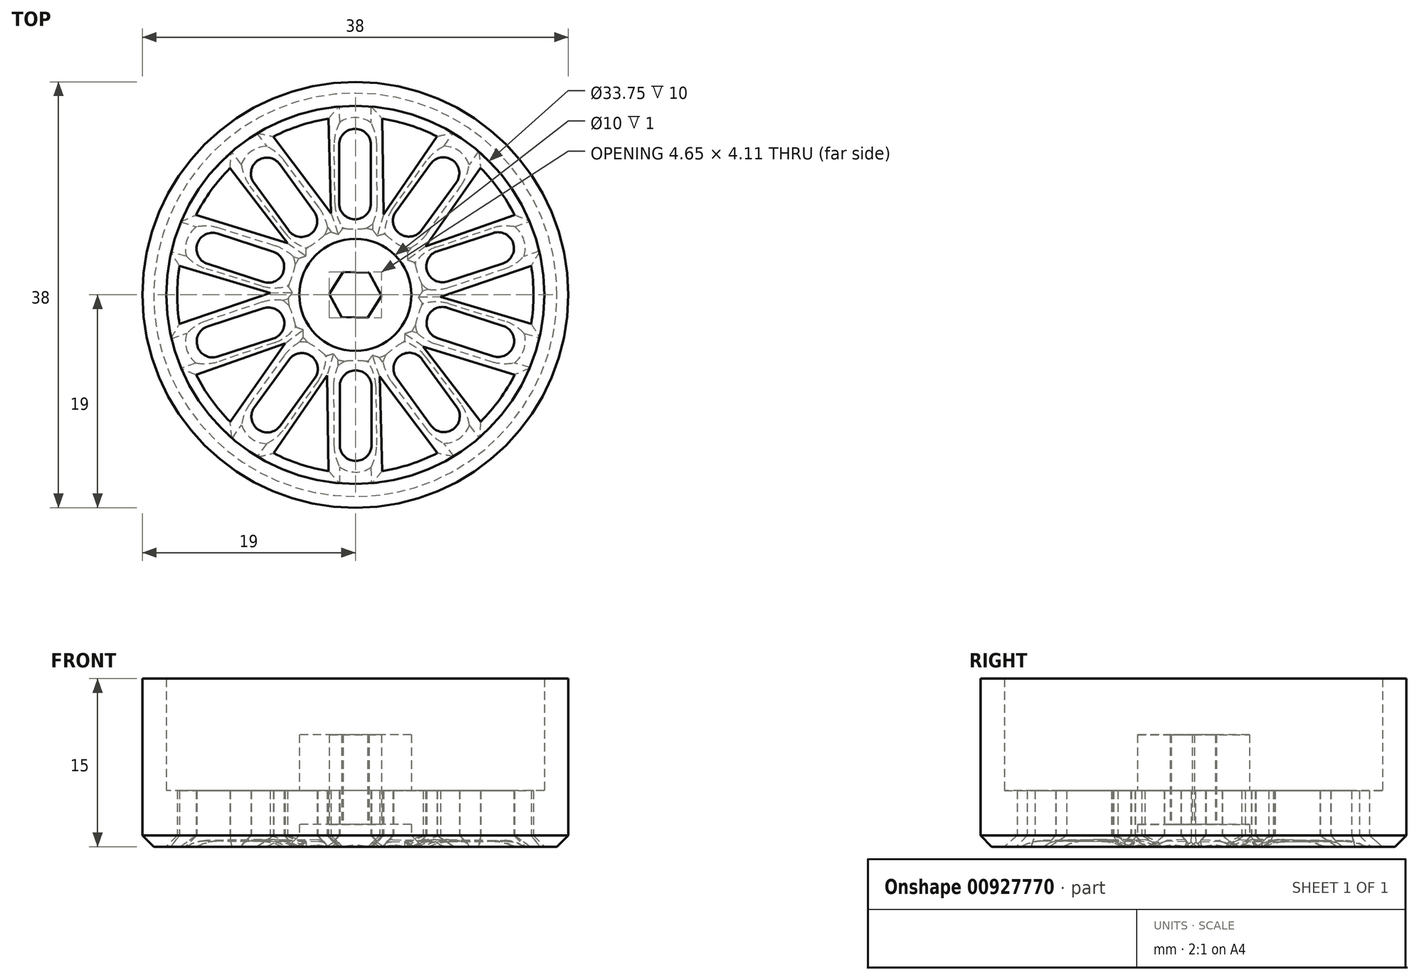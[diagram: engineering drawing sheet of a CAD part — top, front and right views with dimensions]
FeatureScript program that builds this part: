
annotation { "Feature Type Name" : "Feature", "Feature Type Description" : "" }
export const myFeature = defineFeature(function(context is Context, id is Id, definition is map)
    precondition{}
    {
        {
            var Q0;
            Q0=qCreatedBy(makeId("Top.planeOp"),FACE);
            var sketch = newSketch(context, id + "F0", { "sketchPlane" : qUnion([Q0])});
            skCircle(sketch, "E0", {"center": v(0, 0) * mm, "radius": 19 * mm});
            skCircle(sketch, "E1", {"center": v(0, 0) * mm, "radius": 16.88 * mm});
            skCircle(sketch, "E2", {"center": v(0, 0) * mm, "radius": 5 * mm});
            skLineSegment(sketch, "E3", {"start": v(0, 5) * mm, "end": v(0, 16.88) * mm, "construction": true});
            skPoint(sketch, "E4", {"position": v(0, 10.94) * mm});
            skCircle(sketch, "E5", {"center": v(-14.8, 19.1) * mm, "radius": 2.5 * mm});
            skLineSegment(sketch, "E6", {"start": v(-17.26, 19.52) * mm, "end": v(-12.33, 19.52) * mm, "construction": true});
            skLineSegment(sketch, "E7", {"start": v(-15.14, 26.3) * mm, "end": v(-17.26, 19.52) * mm});
            skLineSegment(sketch, "E8", {"start": v(-14.18, 26.28) * mm, "end": v(-12.33, 19.52) * mm});
            skArc(sketch, "E9.filletArc", {"start": v(-14.18, 26.28) * mm, "mid": v(-14.66, 26.65) * mm, "end": v(-15.14, 26.3) * mm});
            skLineSegment(sketch, "E10.5.0", {"start": v(19.08, -22.93) * mm, "end": v(14.42, -19.82) * mm});
            skArc(sketch, "E10.5.1", {"start": v(14.42, -19.82) * mm, "mid": v(13.24, -19.67) * mm, "end": v(12.36, -20.48) * mm});
            skLineSegment(sketch, "E10.5.2", {"start": v(10.23, -25.67) * mm, "end": v(12.36, -20.48) * mm});
            skArc(sketch, "E10.5.3", {"start": v(10.23, -25.67) * mm, "mid": v(14.82, -24.84) * mm, "end": v(19.08, -22.93) * mm});
            skPoint(sketch, "E11", {"position": v(0, 15.9) * mm});
            skCircle(sketch, "E12", {"center": v(0, 0) * mm, "radius": 15.9 * mm, "construction": true});
            skCircle(sketch, "E13", {"center": v(0, 0) * mm, "radius": 5.66 * mm, "construction": true});
            skPoint(sketch, "E14.visualSharp", {"position": v(1.68, 5.4) * mm});
            skArc(sketch, "E15.filletArc", {"start": v(15.09, -4.95) * mm, "mid": v(15.14, -4.92) * mm, "end": v(15.12, -4.86) * mm});
            skArc(sketch, "E16.filletArc", {"start": v(15.12, 4.86) * mm, "mid": v(15.14, 4.92) * mm, "end": v(15.09, 4.95) * mm});
            skLineSegment(sketch, "E17.bottom", {"start": v(1, -18.97) * mm, "end": v(-1, -18.97) * mm, "construction": true});
            skLineSegment(sketch, "E17.top", {"start": v(1, -0.03) * mm, "end": v(-1, -0.03) * mm, "construction": true});
            skLineSegment(sketch, "E18", {"start": v(0, 0) * mm, "end": v(0, -5) * mm, "construction": true});
            skLineSegment(sketch, "E19.trimOffspring", {"start": v(0, -16.88) * mm, "end": v(0, -19) * mm, "construction": true});
            skPoint(sketch, "E20.orphan", {"position": v(0.1, -15.9) * mm});
            skLineSegment(sketch, "E21.bottom", {"start": v(1.45, -13.4) * mm, "end": v(-1.4, -13.4) * mm});
            skLineSegment(sketch, "E21.top", {"start": v(1.45, -8.16) * mm, "end": v(-1.4, -8.16) * mm});
            skLineSegment(sketch, "E21.left", {"start": v(1.45, -13.4) * mm, "end": v(1.45, -8.16) * mm});
            skLineSegment(sketch, "E21.right", {"start": v(-1.4, -13.4) * mm, "end": v(-1.4, -8.16) * mm});
            skPoint(sketch, "E21.middle", {"position": v(0.03, -10.78) * mm});
            skPoint(sketch, "E22.end.orphan", {"position": v(-0.05, -5.66) * mm});
            skCircle(sketch, "E23", {"center": v(0.03, -8.16) * mm, "radius": 1.42 * mm});
            skCircle(sketch, "E24", {"center": v(0.03, -13.4) * mm, "radius": 1.42 * mm});
            skCircle(sketch, "E25.1.0", {"center": v(7.9, -10.83) * mm, "radius": 1.42 * mm});
            skLineSegment(sketch, "E25.1.1", {"start": v(6.75, -11.66) * mm, "end": v(3.67, -7.42) * mm});
            skLineSegment(sketch, "E25.1.2", {"start": v(9.05, -10) * mm, "end": v(5.97, -5.75) * mm});
            skLineSegment(sketch, "E25.1.3", {"start": v(5.97, -5.75) * mm, "end": v(3.67, -7.42) * mm});
            skCircle(sketch, "E25.1.4", {"center": v(4.82, -6.59) * mm, "radius": 1.42 * mm});
            skLineSegment(sketch, "E25.1.5", {"start": v(9.05, -10) * mm, "end": v(6.75, -11.66) * mm});
            skCircle(sketch, "E25.2.0", {"center": v(12.75, -4.12) * mm, "radius": 1.42 * mm});
            skLineSegment(sketch, "E25.2.1", {"start": v(12.31, -5.47) * mm, "end": v(7.33, -3.85) * mm});
            skLineSegment(sketch, "E25.2.2", {"start": v(13.2, -2.77) * mm, "end": v(8.21, -1.15) * mm});
            skLineSegment(sketch, "E25.2.3", {"start": v(8.21, -1.15) * mm, "end": v(7.33, -3.85) * mm});
            skCircle(sketch, "E25.2.4", {"center": v(7.77, -2.5) * mm, "radius": 1.42 * mm});
            skLineSegment(sketch, "E25.2.5", {"start": v(13.2, -2.77) * mm, "end": v(12.31, -5.47) * mm});
            skCircle(sketch, "E25.3.0", {"center": v(12.74, 4.17) * mm, "radius": 1.42 * mm});
            skLineSegment(sketch, "E25.3.1", {"start": v(13.18, 2.82) * mm, "end": v(8.2, 1.2) * mm});
            skLineSegment(sketch, "E25.3.2", {"start": v(12.3, 5.52) * mm, "end": v(7.32, 3.9) * mm});
            skLineSegment(sketch, "E25.3.3", {"start": v(7.32, 3.9) * mm, "end": v(8.2, 1.2) * mm});
            skCircle(sketch, "E25.3.4", {"center": v(7.76, 2.55) * mm, "radius": 1.42 * mm});
            skLineSegment(sketch, "E25.3.5", {"start": v(12.3, 5.52) * mm, "end": v(13.18, 2.82) * mm});
            skCircle(sketch, "E25.4.0", {"center": v(7.86, 10.86) * mm, "radius": 1.42 * mm});
            skLineSegment(sketch, "E25.4.1", {"start": v(9, 10.02) * mm, "end": v(5.93, 5.78) * mm});
            skLineSegment(sketch, "E25.4.2", {"start": v(6.7, 11.7) * mm, "end": v(3.63, 7.45) * mm});
            skLineSegment(sketch, "E25.4.3", {"start": v(3.63, 7.45) * mm, "end": v(5.93, 5.78) * mm});
            skCircle(sketch, "E25.4.4", {"center": v(4.78, 6.62) * mm, "radius": 1.42 * mm});
            skLineSegment(sketch, "E25.4.5", {"start": v(6.7, 11.7) * mm, "end": v(9, 10.02) * mm});
            skCircle(sketch, "E25.5.0", {"center": v(-0.03, 13.4) * mm, "radius": 1.42 * mm});
            skLineSegment(sketch, "E25.5.1", {"start": v(1.4, 13.4) * mm, "end": v(1.4, 8.16) * mm});
            skLineSegment(sketch, "E25.5.2", {"start": v(-1.45, 13.4) * mm, "end": v(-1.45, 8.16) * mm});
            skLineSegment(sketch, "E25.5.3", {"start": v(-1.45, 8.16) * mm, "end": v(1.4, 8.16) * mm});
            skCircle(sketch, "E25.5.4", {"center": v(-0.03, 8.16) * mm, "radius": 1.42 * mm});
            skLineSegment(sketch, "E25.5.5", {"start": v(-1.45, 13.4) * mm, "end": v(1.4, 13.4) * mm});
            skCircle(sketch, "E25.6.0", {"center": v(-7.9, 10.83) * mm, "radius": 1.42 * mm});
            skLineSegment(sketch, "E25.6.1", {"start": v(-6.75, 11.66) * mm, "end": v(-3.67, 7.42) * mm});
            skLineSegment(sketch, "E25.6.2", {"start": v(-9.05, 10) * mm, "end": v(-5.97, 5.75) * mm});
            skLineSegment(sketch, "E25.6.3", {"start": v(-5.97, 5.75) * mm, "end": v(-3.67, 7.42) * mm});
            skCircle(sketch, "E25.6.4", {"center": v(-4.82, 6.59) * mm, "radius": 1.42 * mm});
            skLineSegment(sketch, "E25.6.5", {"start": v(-9.05, 10) * mm, "end": v(-6.75, 11.66) * mm});
            skCircle(sketch, "E25.7.0", {"center": v(-12.75, 4.12) * mm, "radius": 1.42 * mm});
            skLineSegment(sketch, "E25.7.1", {"start": v(-12.31, 5.47) * mm, "end": v(-7.33, 3.85) * mm});
            skLineSegment(sketch, "E25.7.2", {"start": v(-13.2, 2.77) * mm, "end": v(-8.21, 1.15) * mm});
            skLineSegment(sketch, "E25.7.3", {"start": v(-8.21, 1.15) * mm, "end": v(-7.33, 3.85) * mm});
            skCircle(sketch, "E25.7.4", {"center": v(-7.77, 2.5) * mm, "radius": 1.42 * mm});
            skLineSegment(sketch, "E25.7.5", {"start": v(-13.2, 2.77) * mm, "end": v(-12.31, 5.47) * mm});
            skCircle(sketch, "E25.8.0", {"center": v(-12.74, -4.17) * mm, "radius": 1.42 * mm});
            skLineSegment(sketch, "E25.8.1", {"start": v(-13.18, -2.82) * mm, "end": v(-8.2, -1.2) * mm});
            skLineSegment(sketch, "E25.8.2", {"start": v(-12.3, -5.52) * mm, "end": v(-7.32, -3.9) * mm});
            skLineSegment(sketch, "E25.8.3", {"start": v(-7.32, -3.9) * mm, "end": v(-8.2, -1.2) * mm});
            skCircle(sketch, "E25.8.4", {"center": v(-7.76, -2.55) * mm, "radius": 1.42 * mm});
            skLineSegment(sketch, "E25.8.5", {"start": v(-12.3, -5.52) * mm, "end": v(-13.18, -2.82) * mm});
            skLineSegment(sketch, "E26.2.9.0", {"start": v(-9, -10.02) * mm, "end": v(-5.93, -5.78) * mm});
            skCircle(sketch, "E26.3.9.0", {"center": v(-7.86, -10.86) * mm, "radius": 1.42 * mm});
            skLineSegment(sketch, "E26.5.9.0", {"start": v(-6.7, -11.7) * mm, "end": v(-3.63, -7.45) * mm});
            skLineSegment(sketch, "E26.8.9.0", {"start": v(-3.63, -7.45) * mm, "end": v(-5.93, -5.78) * mm});
            skCircle(sketch, "E26.11.9.0", {"center": v(-4.78, -6.62) * mm, "radius": 1.42 * mm});
            skLineSegment(sketch, "E26.13.9.0", {"start": v(-6.7, -11.7) * mm, "end": v(-9, -10.02) * mm});
            skArc(sketch, "E27", {"start": v(-7.3, -14.13) * mm, "mid": v(-4.9, -15.12) * mm, "end": v(-2.39, -15.72) * mm});
            skLineSegment(sketch, "E28", {"start": v(-7.3, -14.13) * mm, "end": v(-2.52, -7.18) * mm});
            skLineSegment(sketch, "E29", {"start": v(-2.52, -7.18) * mm, "end": v(-2.39, -15.72) * mm});
            skLineSegment(sketch, "E30.1.0", {"start": v(2.18, -7.3) * mm, "end": v(7.31, -14.12) * mm});
            skLineSegment(sketch, "E30.1.1", {"start": v(2.4, -15.72) * mm, "end": v(2.18, -7.3) * mm});
            skArc(sketch, "E30.1.2", {"start": v(2.4, -15.72) * mm, "mid": v(4.92, -15.12) * mm, "end": v(7.31, -14.12) * mm});
            skLineSegment(sketch, "E30.2.0", {"start": v(6.05, -4.62) * mm, "end": v(14.22, -7.13) * mm});
            skLineSegment(sketch, "E30.2.1", {"start": v(11.18, -11.3) * mm, "end": v(6.05, -4.62) * mm});
            skArc(sketch, "E30.2.2", {"start": v(11.18, -11.3) * mm, "mid": v(12.86, -9.34) * mm, "end": v(14.22, -7.13) * mm});
            skLineSegment(sketch, "E30.3.0", {"start": v(7.61, -0.18) * mm, "end": v(15.7, 2.6) * mm});
            skLineSegment(sketch, "E30.3.1", {"start": v(15.7, -2.58) * mm, "end": v(7.61, -0.18) * mm});
            skArc(sketch, "E30.3.2", {"start": v(15.7, -2.58) * mm, "mid": v(15.9, 0) * mm, "end": v(15.7, 2.6) * mm});
            skLineSegment(sketch, "E30.4.0", {"start": v(6.26, 4.33) * mm, "end": v(11.17, 11.32) * mm});
            skLineSegment(sketch, "E30.4.1", {"start": v(14.21, 7.14) * mm, "end": v(6.26, 4.33) * mm});
            skArc(sketch, "E30.4.2", {"start": v(14.21, 7.14) * mm, "mid": v(12.86, 9.35) * mm, "end": v(11.17, 11.32) * mm});
            skLineSegment(sketch, "E30.5.0", {"start": v(2.52, 7.18) * mm, "end": v(2.39, 15.72) * mm});
            skLineSegment(sketch, "E30.5.1", {"start": v(7.3, 14.13) * mm, "end": v(2.52, 7.18) * mm});
            skArc(sketch, "E30.5.2", {"start": v(7.3, 14.13) * mm, "mid": v(4.9, 15.12) * mm, "end": v(2.39, 15.72) * mm});
            skLineSegment(sketch, "E30.6.0", {"start": v(-2.18, 7.3) * mm, "end": v(-7.31, 14.12) * mm});
            skLineSegment(sketch, "E30.6.1", {"start": v(-2.4, 15.72) * mm, "end": v(-2.18, 7.3) * mm});
            skArc(sketch, "E30.6.2", {"start": v(-2.4, 15.72) * mm, "mid": v(-4.92, 15.12) * mm, "end": v(-7.31, 14.12) * mm});
            skLineSegment(sketch, "E30.7.0", {"start": v(-6.05, 4.62) * mm, "end": v(-14.22, 7.13) * mm});
            skLineSegment(sketch, "E30.7.1", {"start": v(-11.18, 11.3) * mm, "end": v(-6.05, 4.62) * mm});
            skArc(sketch, "E30.7.2", {"start": v(-11.18, 11.3) * mm, "mid": v(-12.86, 9.34) * mm, "end": v(-14.22, 7.13) * mm});
            skLineSegment(sketch, "E30.8.0", {"start": v(-7.61, 0.18) * mm, "end": v(-15.7, -2.6) * mm});
            skLineSegment(sketch, "E30.8.1", {"start": v(-15.7, 2.58) * mm, "end": v(-7.61, 0.18) * mm});
            skArc(sketch, "E30.8.2", {"start": v(-15.7, 2.58) * mm, "mid": v(-15.9, 0) * mm, "end": v(-15.7, -2.6) * mm});
            skLineSegment(sketch, "E30.9.0", {"start": v(-6.26, -4.33) * mm, "end": v(-11.17, -11.32) * mm});
            skLineSegment(sketch, "E30.9.1", {"start": v(-14.21, -7.14) * mm, "end": v(-6.26, -4.33) * mm});
            skArc(sketch, "E30.9.2", {"start": v(-14.21, -7.14) * mm, "mid": v(-12.86, -9.35) * mm, "end": v(-11.17, -11.32) * mm});
            skSolve(sketch);
        }
        {
            var Q0;
            Q0=makeQuery(id+"F0.imprint","IMPRINT",FACE,{"disambiguationData":[TD([[makeQuery(id+"F0.imprint","IMPRINT",EDGE,{"derivedFrom":sQuery(id+"F0.wireOp",EDGE,"E0")}),1.0]])]});
            extrude(context, id + "F1", {"entities" : qUnion([Q0]), "depth" : 15 * mm, "offsetDistance" : 25 * mm});
        }
        {
            var Q0;
            Q0=makeQuery(id+"F0.imprint","IMPRINT",FACE,{"disambiguationData":[TD([[makeQuery(id+"F0.imprint","IMPRINT",EDGE,{"derivedFrom":sQuery(id+"F0.wireOp",EDGE,"E1")}),1.0]])]});
            extrude(context, id + "F2", {"entities" : qUnion([Q0]), "operationType" : NewBodyOperationType.ADD, "depth" : 5 * mm, "offsetDistance" : 25 * mm});
        }
        {
            var Q0;
            {var subQ0=sQuery(id+"F0.wireOp",EDGE,"E2");var subQ1=makeQuery(id+"F0.imprint","INTERSECT",VERTEX,{"derivedFrom":[subQ0,sQuery(id+"F0.wireOp",EDGE,"FMw9U3Ag-M4uU-eOUw-AIyu-Y3kzjyrUIhWa.right")]});Q0=makeQuery(id+"F0.imprint","IMPRINT",FACE,{"disambiguationData":[TD([[makeQuery(id+"F0.imprint","IMPRINT",EDGE,{"disambiguationData":[TD([[subQ1,1.0]])],"derivedFrom":subQ0}),1.0]])]});}
            extrude(context, id + "F3", {"entities" : qUnion([Q0]), "operationType" : NewBodyOperationType.ADD, "depth" : 10 * mm, "offsetDistance" : 25 * mm});
        }
        {
            var Q0;
            Q0=makeQuery(id+"F0.imprint","IMPRINT",FACE,{"disambiguationData":[TD([[makeQuery(id+"F0.imprint","IMPRINT",EDGE,{"derivedFrom":sQuery(id+"F0.wireOp",EDGE,"E2")}),1.0]])]});
            extrude(context, id + "F4", {"entities" : qUnion([Q0]), "operationType" : NewBodyOperationType.REMOVE, "depth" : 2 * mm, "offsetDistance" : 25 * mm});
        }
        {
            var Q0;
            Q0=makeQuery(id+"F0.imprint","IMPRINT",FACE,{"disambiguationData":[TD([[makeQuery(id+"F0.imprint","IMPRINT",EDGE,{"derivedFrom":sQuery(id+"F0.wireOp",EDGE,"E2")}),1.0]])]});
            var sketch = newSketch(context, id + "F5", { "sketchPlane" : qUnion([Q0])});
            skPoint(sketch, "E31.0.midPoint", {"position": v(-1.32, 0.78) * mm});
            skCircle(sketch, "E32.cCircle", {"center": v(0, 0) * mm, "radius": 2.02 * mm, "construction": true});
            skLineSegment(sketch, "E32.0", {"start": v(-2.33, 0.08) * mm, "end": v(-1.1, 2.06) * mm});
            skLineSegment(sketch, "E32.1", {"start": v(-1.1, 2.06) * mm, "end": v(1.24, 1.97) * mm});
            skLineSegment(sketch, "E32.2", {"start": v(1.24, 1.97) * mm, "end": v(2.33, -0.08) * mm});
            skLineSegment(sketch, "E32.3", {"start": v(2.33, -0.08) * mm, "end": v(1.1, -2.06) * mm});
            skLineSegment(sketch, "E32.4", {"start": v(1.1, -2.06) * mm, "end": v(-1.24, -1.97) * mm});
            skLineSegment(sketch, "E32.5", {"start": v(-1.24, -1.97) * mm, "end": v(-2.33, 0.08) * mm});
            skPoint(sketch, "E32.0.midPoint", {"position": v(-1.7, 1.07) * mm});
            skPoint(sketch, "E33.orphan", {"position": v(-0.9, -1.52) * mm});
            skPoint(sketch, "E34.orphan", {"position": v(0.87, -1.54) * mm});
            skPoint(sketch, "E35.orphan", {"position": v(-1.77, 0.02) * mm});
            skPoint(sketch, "E31.1.start.orphan", {"position": v(-0.87, 1.54) * mm});
            skCircle(sketch, "E36.cCircle", {"center": v(0, -5.83) * mm, "radius": 1.3 * mm, "construction": true});
            skLineSegment(sketch, "E36.0", {"start": v(0.95, -7.14) * mm, "end": v(-0.95, -7.14) * mm});
            skLineSegment(sketch, "E36.1", {"start": v(-0.95, -7.14) * mm, "end": v(-1.54, -5.33) * mm});
            skLineSegment(sketch, "E36.2", {"start": v(-1.54, -5.33) * mm, "end": v(0, -4.21) * mm});
            skLineSegment(sketch, "E36.3", {"start": v(0, -4.21) * mm, "end": v(1.54, -5.33) * mm});
            skLineSegment(sketch, "E36.4", {"start": v(1.54, -5.33) * mm, "end": v(0.95, -7.14) * mm});
            skPoint(sketch, "E36.0.midPoint", {"position": v(0, -7.14) * mm});
            skLineSegment(sketch, "E37.1.0", {"start": v(5.54, -0.18) * mm, "end": v(7.08, -1.3) * mm});
            skLineSegment(sketch, "E37.1.1", {"start": v(4, -1.3) * mm, "end": v(5.54, -0.18) * mm});
            skLineSegment(sketch, "E37.1.2", {"start": v(4.6, -3.11) * mm, "end": v(4, -1.3) * mm});
            skLineSegment(sketch, "E37.1.3", {"start": v(6.5, -3.11) * mm, "end": v(4.6, -3.11) * mm});
            skLineSegment(sketch, "E37.1.4", {"start": v(7.08, -1.3) * mm, "end": v(6.5, -3.11) * mm});
            skLineSegment(sketch, "E37.2.0", {"start": v(1.89, 5.22) * mm, "end": v(3.43, 6.33) * mm});
            skLineSegment(sketch, "E37.2.1", {"start": v(2.47, 3.4) * mm, "end": v(1.89, 5.22) * mm});
            skLineSegment(sketch, "E37.2.2", {"start": v(4.38, 3.4) * mm, "end": v(2.47, 3.4) * mm});
            skLineSegment(sketch, "E37.2.3", {"start": v(4.97, 5.22) * mm, "end": v(4.38, 3.4) * mm});
            skLineSegment(sketch, "E37.2.4", {"start": v(3.43, 6.33) * mm, "end": v(4.97, 5.22) * mm});
            skLineSegment(sketch, "E37.3.0", {"start": v(-4.38, 3.4) * mm, "end": v(-4.97, 5.22) * mm});
            skLineSegment(sketch, "E37.3.1", {"start": v(-2.47, 3.4) * mm, "end": v(-4.38, 3.4) * mm});
            skLineSegment(sketch, "E37.3.2", {"start": v(-1.89, 5.22) * mm, "end": v(-2.47, 3.4) * mm});
            skLineSegment(sketch, "E37.3.3", {"start": v(-3.43, 6.33) * mm, "end": v(-1.89, 5.22) * mm});
            skLineSegment(sketch, "E37.3.4", {"start": v(-4.97, 5.22) * mm, "end": v(-3.43, 6.33) * mm});
            skLineSegment(sketch, "E37.4.0", {"start": v(-4.6, -3.11) * mm, "end": v(-6.5, -3.11) * mm});
            skLineSegment(sketch, "E37.4.1", {"start": v(-4, -1.3) * mm, "end": v(-4.6, -3.11) * mm});
            skLineSegment(sketch, "E37.4.2", {"start": v(-5.54, -0.18) * mm, "end": v(-4, -1.3) * mm});
            skLineSegment(sketch, "E37.4.3", {"start": v(-7.08, -1.3) * mm, "end": v(-5.54, -0.18) * mm});
            skLineSegment(sketch, "E37.4.4", {"start": v(-6.5, -3.11) * mm, "end": v(-7.08, -1.3) * mm});
            skSolve(sketch);
        }
        {
            var Q0;
            Q0=makeQuery(id+"F5.imprint","IMPRINT",FACE,{"disambiguationData":[TD([[makeQuery(id+"F5.imprint","IMPRINT",EDGE,{"derivedFrom":sQuery(id+"F5.wireOp",EDGE,"E32.0")}),-1.0]])]});
            extrude(context, id + "F6", {"entities" : qUnion([Q0]), "operationType" : NewBodyOperationType.REMOVE, "depth" : 25 * mm, "offsetDistance" : 25 * mm});
        }
        {
            var Q0;
            {var subQ0=sQuery(id+"F0.wireOp",EDGE,"E2");var subQ1=sQuery(id+"F0.wireOp",EDGE,"E1");Q0=makeQuery(id+"F3.boolean.opBoolean","MERGE",FACE,{"derivedFrom":[makeQuery(id+"F2.boolean.opBoolean","MERGE",FACE,{"derivedFrom":[makeQuery(id+"F1.opExtrude","CAP_FACE",FACE,{"disambiguationData":[OSD([sQuery(id+"F0.wireOp",EDGE,"E0"),subQ1])],"isStart":true}),makeQuery(id+"F2.opExtrude","CAP_FACE",FACE,{"disambiguationData":[OSD([subQ1,subQ0,sQuery(id+"F0.wireOp",EDGE,"E5"),sQuery(id+"F0.wireOp",EDGE,"E7"),sQuery(id+"F0.wireOp",EDGE,"E8"),sQuery(id+"F0.wireOp",EDGE,"E9.filletArc"),sQuery(id+"F0.wireOp",EDGE,"1d552ee7-da9b-4f0c-a288-42d00aae1e59.1.0"),sQuery(id+"F0.wireOp",EDGE,"1d552ee7-da9b-4f0c-a288-42d00aae1e59.1.1"),sQuery(id+"F0.wireOp",EDGE,"1d552ee7-da9b-4f0c-a288-42d00aae1e59.1.2"),sQuery(id+"F0.wireOp",EDGE,"1d552ee7-da9b-4f0c-a288-42d00aae1e59.1.3"),sQuery(id+"F0.wireOp",EDGE,"1d552ee7-da9b-4f0c-a288-42d00aae1e59.2.0"),sQuery(id+"F0.wireOp",EDGE,"1d552ee7-da9b-4f0c-a288-42d00aae1e59.2.1"),sQuery(id+"F0.wireOp",EDGE,"1d552ee7-da9b-4f0c-a288-42d00aae1e59.2.2"),sQuery(id+"F0.wireOp",EDGE,"1d552ee7-da9b-4f0c-a288-42d00aae1e59.2.3"),sQuery(id+"F0.wireOp",EDGE,"1d552ee7-da9b-4f0c-a288-42d00aae1e59.3.0"),sQuery(id+"F0.wireOp",EDGE,"1d552ee7-da9b-4f0c-a288-42d00aae1e59.3.1"),sQuery(id+"F0.wireOp",EDGE,"1d552ee7-da9b-4f0c-a288-42d00aae1e59.3.2"),sQuery(id+"F0.wireOp",EDGE,"1d552ee7-da9b-4f0c-a288-42d00aae1e59.3.3"),sQuery(id+"F0.wireOp",EDGE,"1d552ee7-da9b-4f0c-a288-42d00aae1e59.4.0"),sQuery(id+"F0.wireOp",EDGE,"1d552ee7-da9b-4f0c-a288-42d00aae1e59.4.1"),sQuery(id+"F0.wireOp",EDGE,"1d552ee7-da9b-4f0c-a288-42d00aae1e59.4.2"),sQuery(id+"F0.wireOp",EDGE,"1d552ee7-da9b-4f0c-a288-42d00aae1e59.4.3"),sQuery(id+"F0.wireOp",EDGE,"1d552ee7-da9b-4f0c-a288-42d00aae1e59.5.0"),sQuery(id+"F0.wireOp",EDGE,"1d552ee7-da9b-4f0c-a288-42d00aae1e59.5.1"),sQuery(id+"F0.wireOp",EDGE,"1d552ee7-da9b-4f0c-a288-42d00aae1e59.5.2"),sQuery(id+"F0.wireOp",EDGE,"1d552ee7-da9b-4f0c-a288-42d00aae1e59.5.3"),sQuery(id+"F0.wireOp",EDGE,"1d552ee7-da9b-4f0c-a288-42d00aae1e59.6.0"),sQuery(id+"F0.wireOp",EDGE,"1d552ee7-da9b-4f0c-a288-42d00aae1e59.6.1"),sQuery(id+"F0.wireOp",EDGE,"1d552ee7-da9b-4f0c-a288-42d00aae1e59.6.2"),sQuery(id+"F0.wireOp",EDGE,"1d552ee7-da9b-4f0c-a288-42d00aae1e59.6.3"),sQuery(id+"F0.wireOp",EDGE,"1d552ee7-da9b-4f0c-a288-42d00aae1e59.7.0"),sQuery(id+"F0.wireOp",EDGE,"1d552ee7-da9b-4f0c-a288-42d00aae1e59.7.1"),sQuery(id+"F0.wireOp",EDGE,"1d552ee7-da9b-4f0c-a288-42d00aae1e59.7.2"),sQuery(id+"F0.wireOp",EDGE,"1d552ee7-da9b-4f0c-a288-42d00aae1e59.7.3"),sQuery(id+"F0.wireOp",EDGE,"1d552ee7-da9b-4f0c-a288-42d00aae1e59.8.0"),sQuery(id+"F0.wireOp",EDGE,"1d552ee7-da9b-4f0c-a288-42d00aae1e59.8.1"),sQuery(id+"F0.wireOp",EDGE,"1d552ee7-da9b-4f0c-a288-42d00aae1e59.8.2"),sQuery(id+"F0.wireOp",EDGE,"1d552ee7-da9b-4f0c-a288-42d00aae1e59.8.3"),sQuery(id+"F0.wireOp",EDGE,"1d552ee7-da9b-4f0c-a288-42d00aae1e59.9.0"),sQuery(id+"F0.wireOp",EDGE,"1d552ee7-da9b-4f0c-a288-42d00aae1e59.9.1"),sQuery(id+"F0.wireOp",EDGE,"1d552ee7-da9b-4f0c-a288-42d00aae1e59.9.2"),sQuery(id+"F0.wireOp",EDGE,"1d552ee7-da9b-4f0c-a288-42d00aae1e59.9.3"),sQuery(id+"F0.wireOp",EDGE,"dG9ruqm5-QT7Y-QHdv-tEC1-1vZ8V0C7jhKi"),sQuery(id+"F0.wireOp",EDGE,"13zynFo3-rpzZ-Hc7Q-yODg-0hWWHLczEeh4"),sQuery(id+"F0.wireOp",EDGE,"LefVzuDw-nWrM-VCjd-qSRF-Sznb41wakj4H"),sQuery(id+"F0.wireOp",EDGE,"FdDrVg9r-qZOv-yWwV-fWKn-j6eQ8j2AcD15"),sQuery(id+"F0.wireOp",EDGE,"E10.1.0"),sQuery(id+"F0.wireOp",EDGE,"E10.1.1"),sQuery(id+"F0.wireOp",EDGE,"E10.1.2"),sQuery(id+"F0.wireOp",EDGE,"E10.1.3"),sQuery(id+"F0.wireOp",EDGE,"E10.2.0"),sQuery(id+"F0.wireOp",EDGE,"E10.2.1"),sQuery(id+"F0.wireOp",EDGE,"E10.2.2"),sQuery(id+"F0.wireOp",EDGE,"E10.2.3"),sQuery(id+"F0.wireOp",EDGE,"E10.3.0"),sQuery(id+"F0.wireOp",EDGE,"E10.3.1"),sQuery(id+"F0.wireOp",EDGE,"E10.3.2"),sQuery(id+"F0.wireOp",EDGE,"E10.3.3"),sQuery(id+"F0.wireOp",EDGE,"E10.4.0"),sQuery(id+"F0.wireOp",EDGE,"E10.4.1"),sQuery(id+"F0.wireOp",EDGE,"E10.4.2"),sQuery(id+"F0.wireOp",EDGE,"E10.4.3"),sQuery(id+"F0.wireOp",EDGE,"E10.5.0"),sQuery(id+"F0.wireOp",EDGE,"E10.5.1"),sQuery(id+"F0.wireOp",EDGE,"E10.5.2"),sQuery(id+"F0.wireOp",EDGE,"E10.5.3"),sQuery(id+"F0.wireOp",EDGE,"E10.6.0"),sQuery(id+"F0.wireOp",EDGE,"E10.6.1"),sQuery(id+"F0.wireOp",EDGE,"E10.6.2"),sQuery(id+"F0.wireOp",EDGE,"E10.6.3"),sQuery(id+"F0.wireOp",EDGE,"E10.7.0"),sQuery(id+"F0.wireOp",EDGE,"E10.7.1"),sQuery(id+"F0.wireOp",EDGE,"E10.7.2"),sQuery(id+"F0.wireOp",EDGE,"E10.7.3"),sQuery(id+"F0.wireOp",EDGE,"E10.8.0"),sQuery(id+"F0.wireOp",EDGE,"E10.8.1"),sQuery(id+"F0.wireOp",EDGE,"E10.8.2"),sQuery(id+"F0.wireOp",EDGE,"E10.8.3"),sQuery(id+"F0.wireOp",EDGE,"E10.9.0"),sQuery(id+"F0.wireOp",EDGE,"E10.9.1"),sQuery(id+"F0.wireOp",EDGE,"E10.9.2"),sQuery(id+"F0.wireOp",EDGE,"E10.9.3")])],"isStart":true})]}),makeQuery(id+"F3.opExtrude","CAP_FACE",FACE,{"disambiguationData":[OSD([subQ0])],"isStart":true})]});}
            chamfer(context, id + "F7", {"entities" : qUnion([Q0]), "chamferType" : ChamferType.TWO_OFFSETS, "width1" : 1 * mm, "oppositeDirection" : false, "width2" : 1 * mm, "tangentPropagation" : true});
        }
    });
